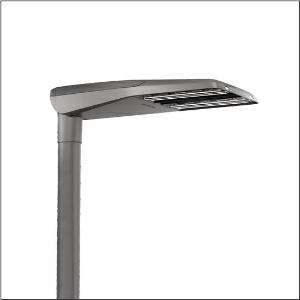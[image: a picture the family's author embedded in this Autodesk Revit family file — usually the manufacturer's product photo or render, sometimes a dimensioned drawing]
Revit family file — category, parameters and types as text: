
# Revit family: streetlight_sl_11_iq_midi___st1_2a_5xc3a11f08me_159a
name_source: partatom
category: Lighting Fixtures
units: mm (PartAtom-declared; Revit-internal decimal feet)

## family parameters
Cut with Voids When Loaded = No
Host = Face
Light Source = No
Part Type = Normal
Room Calculation Point = No
Round Connector Dimension = Use Diameter
Shared = No

## types (1)
- --- (1 x LED, 11170 lm, 124.5 W, 1800K)
    Apparent Load = 125 VA
    CIE Flux Codes = 32 70 96 100 100
    Color Rendering = 70
    Color Temperature = 1800K
    Default Elevation = 1800 mm  [stored 5.90551 ft]
    Description = Streetlight SL 11 iQ midi, mast luminaire, primary light control with 3 zone facetted reflector, of plastic, silver coated, highly specular, primary optical cover: cover, of PMMA, transparent, light distribution: ST1.2a, light emission: direct distribution, primary light characteristic: asymmetric, installation type: post-top, side-entry, LED, High Power LED, rated luminous flux: 11.170lm, luminous efficacy: 90lm/W, light colour: 718, colour temperature: 1800K, control: Street-Remote, Auto-Match, Temp-Guard, Lumen-Switch, Night-Set, Smart-Wire, Light-Fading, Desk-Remote (wireless, voltage-free reading and setting of iQ features in the workshop via application-optimized NFC function/RFID function), optimised constant luminous flux control (CLO 2.0), with cable H07RN-F 5x 1.5mm², mains connection: 230..240V, AC, 50/60Hz, connection cable pre-assembled, cable length: 12,5m, start of lifetime: 125W, end of service life: 132W, reduction: 55W, luminaire housing, of diecast aluminium, powder-coated, Siteco® metallic grey (DB 702S), please order mast flange separately, inclination adjustable without tools: 0°, 5°, 10°, 15° (post-top) | 0°, -5°, -10°, -15° (side-entry), sealing non-destructively replaceable, multi-level sealing system, length: 780mm, width: 376mm, height: 118mm, mast flange for spigot size: 42mm (side-entry): 5XC10008XM4, 60/48mm (side-entry/post-top): 5XC10108XM2, 76/60mm (side-entry/post-top): 5XC10108XM1, equipment: Power, protection rating (complete): IP66, insulation class (complete): insulation class II (safety insulation), certification: CE, ENEC, VDE, impact resistance: IK09, permissible operating ambient temperature for outdoor applications: -25..+50°C, standard-compliant lighting for roads and squares, Environmental Product Declaration (EPD) tested and certified by an independent institute, packaging unit: 1 piece

Light Distribution: ST1.2a
    Height = 118 mm
    Lamp = 1 x LED
    Lamp Light Flux = 11170 lm
    Lamp Power = 124.5 W
    Lamp count = 1
    Length = 780 mm
    Luminous efficacy = 90 lm/W
    Manufacturer = Siteco
    ModVariant = No
    Model = 5XC3A11F08ME
    Number of Poles = 1
    OnlyDefault = Yes
    Power Factor = 1
    Product Name = Streetlight SL 11 iQ midi | ST1.2a
    Product group = mast luminaire | pylon top
    ProductGroupID = 6100
    Protection Class = Protection class II
    Protection Degree = IP 66
    RLX_Detail_Level = 1
    RLX_Emergency_Light_Flux = 0 lm
    RLX_Emergency_Type = 0
    RLX_Emergency_Type_DB = No
    RlxData = <blob elided: 70793 chars, md5=f2c6600f>
    Socket = socket
    Standby Power = 0 W
    System Light Flux = 11170 lm
    System Power = 125 W
    Type Comments = factory setting: luminous flux: 100 % | dim-lin: 254 | 554 mA
    Type Image = l_1005960.jpg
    URL = http://relux.com
    VarID = @adj_010575
    Voltage = 0 V
    Weight = 0.00 kg
    Width = 376 mm

note: [stored X ft] marks values corroborated as IEEE doubles in the binary element streams (Revit-internal decimal feet)

## geometry (parser evidence)
native form markers: Blend x4, Sweep x10
no freeform markers — native parametric forms only
